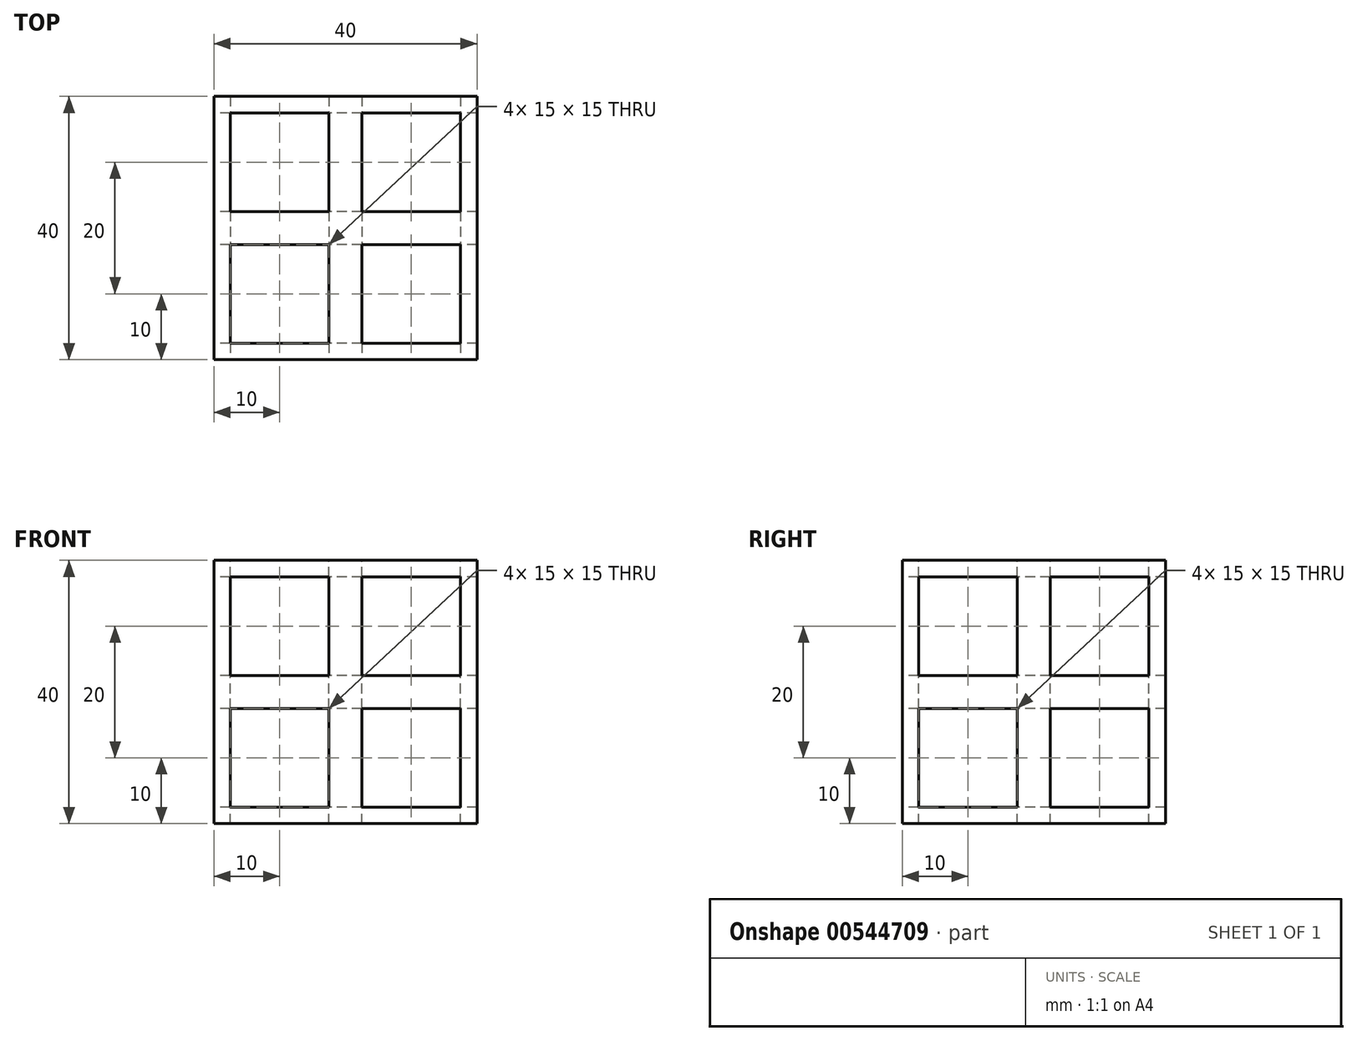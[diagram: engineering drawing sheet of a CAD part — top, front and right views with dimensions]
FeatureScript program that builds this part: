
annotation { "Feature Type Name" : "Feature", "Feature Type Description" : "" }
export const myFeature = defineFeature(function(context is Context, id is Id, definition is map)
    precondition{}
    {
        {
            var Q0;
            Q0=qCreatedBy(makeId("Front.planeOp"),FACE);
            var sketch = newSketch(context, id + "F0", { "sketchPlane" : qUnion([Q0])});
            skLineSegment(sketch, "E0.bottom", {"start": v(20, -20) * mm, "end": v(-20, -20) * mm});
            skLineSegment(sketch, "E0.top", {"start": v(20, 20) * mm, "end": v(-20, 20) * mm});
            skLineSegment(sketch, "E0.left", {"start": v(20, -20) * mm, "end": v(20, 20) * mm});
            skLineSegment(sketch, "E0.right", {"start": v(-20, -20) * mm, "end": v(-20, 20) * mm});
            skPoint(sketch, "E0.middle", {"position": v(0, 0) * mm});
            skSolve(sketch);
        }
        {
            var Q0;
            Q0=makeQuery(id+"F0.imprint","IMPRINT",FACE,{"disambiguationData":[TD([[makeQuery(id+"F0.imprint","IMPRINT",EDGE,{"derivedFrom":sQuery(id+"F0.wireOp",EDGE,"E0.bottom")}),-1.0]])]});
            extrude(context, id + "F1", {"entities" : qUnion([Q0]), "depth" : 40 * mm, "offsetDistance" : 25 * mm});
        }
        {
            var Q0;
            Q0=makeQuery(id+"F1.opExtrude","CAP_FACE",FACE,{"disambiguationData":[OSD([sQuery(id+"F0.wireOp",EDGE,"E0.bottom"),sQuery(id+"F0.wireOp",EDGE,"E0.top"),sQuery(id+"F0.wireOp",EDGE,"E0.left"),sQuery(id+"F0.wireOp",EDGE,"E0.right")])],"isStart":false});
            var sketch = newSketch(context, id + "F2", { "sketchPlane" : qUnion([Q0])});
            skPoint(sketch, "E1", {"position": v(-10, 10) * mm});
            skPoint(sketch, "E2", {"position": v(10, 10) * mm});
            skPoint(sketch, "E3", {"position": v(10, -10) * mm});
            skPoint(sketch, "E4", {"position": v(-10, -10) * mm});
            skLineSegment(sketch, "E5.bottom", {"start": v(-2.5, 2.5) * mm, "end": v(-17.5, 2.5) * mm});
            skLineSegment(sketch, "E5.top", {"start": v(-2.5, 17.5) * mm, "end": v(-17.5, 17.5) * mm});
            skLineSegment(sketch, "E5.left", {"start": v(-2.5, 2.5) * mm, "end": v(-2.5, 17.5) * mm});
            skLineSegment(sketch, "E5.right", {"start": v(-17.5, 2.5) * mm, "end": v(-17.5, 17.5) * mm});
            skLineSegment(sketch, "E6.bottom", {"start": v(17.5, 2.5) * mm, "end": v(2.5, 2.5) * mm});
            skLineSegment(sketch, "E6.top", {"start": v(17.5, 17.5) * mm, "end": v(2.5, 17.5) * mm});
            skLineSegment(sketch, "E6.left", {"start": v(17.5, 2.5) * mm, "end": v(17.5, 17.5) * mm});
            skLineSegment(sketch, "E6.right", {"start": v(2.5, 2.5) * mm, "end": v(2.5, 17.5) * mm});
            skLineSegment(sketch, "E7.bottom", {"start": v(-2.5, -17.5) * mm, "end": v(-17.5, -17.5) * mm});
            skLineSegment(sketch, "E7.top", {"start": v(-2.5, -2.5) * mm, "end": v(-17.5, -2.5) * mm});
            skLineSegment(sketch, "E7.left", {"start": v(-2.5, -17.5) * mm, "end": v(-2.5, -2.5) * mm});
            skLineSegment(sketch, "E7.right", {"start": v(-17.5, -17.5) * mm, "end": v(-17.5, -2.5) * mm});
            skLineSegment(sketch, "E8.bottom", {"start": v(17.5, -17.5) * mm, "end": v(2.5, -17.5) * mm});
            skLineSegment(sketch, "E8.top", {"start": v(17.5, -2.5) * mm, "end": v(2.5, -2.5) * mm});
            skLineSegment(sketch, "E8.left", {"start": v(17.5, -17.5) * mm, "end": v(17.5, -2.5) * mm});
            skLineSegment(sketch, "E8.right", {"start": v(2.5, -17.5) * mm, "end": v(2.5, -2.5) * mm});
            skSolve(sketch);
        }
        {
            var Q0;
            Q0=makeQuery(id+"F2.imprint","IMPRINT",FACE,{"disambiguationData":[TD([[makeQuery(id+"F2.imprint","IMPRINT",EDGE,{"derivedFrom":sQuery(id+"F2.wireOp",EDGE,"E5.bottom")}),-1.0]])]});
            var Q1;
            Q1=makeQuery(id+"F2.imprint","IMPRINT",FACE,{"disambiguationData":[TD([[makeQuery(id+"F2.imprint","IMPRINT",EDGE,{"derivedFrom":sQuery(id+"F2.wireOp",EDGE,"E6.bottom")}),-1.0]])]});
            var Q2;
            Q2=makeQuery(id+"F2.imprint","IMPRINT",FACE,{"disambiguationData":[TD([[makeQuery(id+"F2.imprint","IMPRINT",EDGE,{"derivedFrom":sQuery(id+"F2.wireOp",EDGE,"E7.bottom")}),-1.0]])]});
            var Q3;
            Q3=makeQuery(id+"F2.imprint","IMPRINT",FACE,{"disambiguationData":[TD([[makeQuery(id+"F2.imprint","IMPRINT",EDGE,{"derivedFrom":sQuery(id+"F2.wireOp",EDGE,"E8.bottom")}),-1.0]])]});
            extrude(context, id + "F3", {"entities" : qUnion([Q0, Q1, Q2, Q3]), "operationType" : NewBodyOperationType.REMOVE, "endBound" : BoundingType.THROUGH_ALL, "oppositeDirection" : true, "depth" : 25 * mm, "offsetDistance" : 25 * mm});
        }
        {
            var Q0;
            Q0=makeQuery(id+"F1.opExtrude","SWEPT_FACE",FACE,{"disambiguationData":[OSD([sQuery(id+"F0.wireOp",EDGE,"E0.right")])]});
            var sketch = newSketch(context, id + "F4", { "sketchPlane" : qUnion([Q0])});
            skPoint(sketch, "E9", {"position": v(10, 10) * mm});
            skPoint(sketch, "E10", {"position": v(30, 10) * mm});
            skPoint(sketch, "E11", {"position": v(30, -10) * mm});
            skPoint(sketch, "E12", {"position": v(10, -10) * mm});
            skLineSegment(sketch, "E13.bottom", {"start": v(17.5, 2.5) * mm, "end": v(2.5, 2.5) * mm});
            skLineSegment(sketch, "E13.top", {"start": v(17.5, 17.5) * mm, "end": v(2.5, 17.5) * mm});
            skLineSegment(sketch, "E13.left", {"start": v(17.5, 2.5) * mm, "end": v(17.5, 17.5) * mm});
            skLineSegment(sketch, "E13.right", {"start": v(2.5, 2.5) * mm, "end": v(2.5, 17.5) * mm});
            skLineSegment(sketch, "E14.bottom", {"start": v(37.5, 2.5) * mm, "end": v(22.5, 2.5) * mm});
            skLineSegment(sketch, "E14.top", {"start": v(37.5, 17.5) * mm, "end": v(22.5, 17.5) * mm});
            skLineSegment(sketch, "E14.left", {"start": v(37.5, 2.5) * mm, "end": v(37.5, 17.5) * mm});
            skLineSegment(sketch, "E14.right", {"start": v(22.5, 2.5) * mm, "end": v(22.5, 17.5) * mm});
            skLineSegment(sketch, "E15.bottom", {"start": v(17.5, -17.5) * mm, "end": v(2.5, -17.5) * mm});
            skLineSegment(sketch, "E15.top", {"start": v(17.5, -2.5) * mm, "end": v(2.5, -2.5) * mm});
            skLineSegment(sketch, "E15.left", {"start": v(17.5, -17.5) * mm, "end": v(17.5, -2.5) * mm});
            skLineSegment(sketch, "E15.right", {"start": v(2.5, -17.5) * mm, "end": v(2.5, -2.5) * mm});
            skLineSegment(sketch, "E16.bottom", {"start": v(37.5, -17.5) * mm, "end": v(22.5, -17.5) * mm});
            skLineSegment(sketch, "E16.top", {"start": v(37.5, -2.5) * mm, "end": v(22.5, -2.5) * mm});
            skLineSegment(sketch, "E16.left", {"start": v(37.5, -17.5) * mm, "end": v(37.5, -2.5) * mm});
            skLineSegment(sketch, "E16.right", {"start": v(22.5, -17.5) * mm, "end": v(22.5, -2.5) * mm});
            skSolve(sketch);
        }
        {
            var Q0;
            Q0=makeQuery(id+"F4.imprint","IMPRINT",FACE,{"disambiguationData":[TD([[makeQuery(id+"F4.imprint","IMPRINT",EDGE,{"derivedFrom":sQuery(id+"F4.wireOp",EDGE,"E13.bottom")}),-1.0]])]});
            var Q1;
            Q1=makeQuery(id+"F4.imprint","IMPRINT",FACE,{"disambiguationData":[TD([[makeQuery(id+"F4.imprint","IMPRINT",EDGE,{"derivedFrom":sQuery(id+"F4.wireOp",EDGE,"E14.bottom")}),-1.0]])]});
            var Q2;
            Q2=makeQuery(id+"F4.imprint","IMPRINT",FACE,{"disambiguationData":[TD([[makeQuery(id+"F4.imprint","IMPRINT",EDGE,{"derivedFrom":sQuery(id+"F4.wireOp",EDGE,"E15.bottom")}),-1.0]])]});
            var Q3;
            Q3=makeQuery(id+"F4.imprint","IMPRINT",FACE,{"disambiguationData":[TD([[makeQuery(id+"F4.imprint","IMPRINT",EDGE,{"derivedFrom":sQuery(id+"F4.wireOp",EDGE,"E16.bottom")}),-1.0]])]});
            extrude(context, id + "F5", {"entities" : qUnion([Q0, Q1, Q2, Q3]), "operationType" : NewBodyOperationType.REMOVE, "endBound" : BoundingType.THROUGH_ALL, "oppositeDirection" : true, "depth" : 25 * mm, "offsetDistance" : 25 * mm});
        }
        {
            var Q0;
            Q0=makeQuery(id+"F1.opExtrude","SWEPT_FACE",FACE,{"disambiguationData":[OSD([sQuery(id+"F0.wireOp",EDGE,"E0.top")])]});
            var sketch = newSketch(context, id + "F6", { "sketchPlane" : qUnion([Q0])});
            skPoint(sketch, "E17", {"position": v(-10, -10) * mm});
            skPoint(sketch, "E18", {"position": v(10, -10) * mm});
            skPoint(sketch, "E19", {"position": v(10, -30) * mm});
            skPoint(sketch, "E20", {"position": v(-10, -30) * mm});
            skLineSegment(sketch, "E21.bottom", {"start": v(-2.5, -17.5) * mm, "end": v(-17.5, -17.5) * mm});
            skLineSegment(sketch, "E21.top", {"start": v(-2.5, -2.5) * mm, "end": v(-17.5, -2.5) * mm});
            skLineSegment(sketch, "E21.left", {"start": v(-2.5, -17.5) * mm, "end": v(-2.5, -2.5) * mm});
            skLineSegment(sketch, "E21.right", {"start": v(-17.5, -17.5) * mm, "end": v(-17.5, -2.5) * mm});
            skLineSegment(sketch, "E22.bottom", {"start": v(17.5, -17.5) * mm, "end": v(2.5, -17.5) * mm});
            skLineSegment(sketch, "E22.top", {"start": v(17.5, -2.5) * mm, "end": v(2.5, -2.5) * mm});
            skLineSegment(sketch, "E22.left", {"start": v(17.5, -17.5) * mm, "end": v(17.5, -2.5) * mm});
            skLineSegment(sketch, "E22.right", {"start": v(2.5, -17.5) * mm, "end": v(2.5, -2.5) * mm});
            skLineSegment(sketch, "E23.bottom", {"start": v(-2.5, -37.5) * mm, "end": v(-17.5, -37.5) * mm});
            skLineSegment(sketch, "E23.top", {"start": v(-2.5, -22.5) * mm, "end": v(-17.5, -22.5) * mm});
            skLineSegment(sketch, "E23.left", {"start": v(-2.5, -37.5) * mm, "end": v(-2.5, -22.5) * mm});
            skLineSegment(sketch, "E23.right", {"start": v(-17.5, -37.5) * mm, "end": v(-17.5, -22.5) * mm});
            skLineSegment(sketch, "E24.bottom", {"start": v(17.5, -37.5) * mm, "end": v(2.5, -37.5) * mm});
            skLineSegment(sketch, "E24.top", {"start": v(17.5, -22.5) * mm, "end": v(2.5, -22.5) * mm});
            skLineSegment(sketch, "E24.left", {"start": v(17.5, -37.5) * mm, "end": v(17.5, -22.5) * mm});
            skLineSegment(sketch, "E24.right", {"start": v(2.5, -37.5) * mm, "end": v(2.5, -22.5) * mm});
            skSolve(sketch);
        }
        {
            var Q0;
            Q0=makeQuery(id+"F6.imprint","IMPRINT",FACE,{"disambiguationData":[TD([[makeQuery(id+"F6.imprint","IMPRINT",EDGE,{"derivedFrom":sQuery(id+"F6.wireOp",EDGE,"E21.bottom")}),-1.0]])]});
            var Q1;
            Q1=makeQuery(id+"F6.imprint","IMPRINT",FACE,{"disambiguationData":[TD([[makeQuery(id+"F6.imprint","IMPRINT",EDGE,{"derivedFrom":sQuery(id+"F6.wireOp",EDGE,"E22.bottom")}),-1.0]])]});
            var Q2;
            Q2=makeQuery(id+"F6.imprint","IMPRINT",FACE,{"disambiguationData":[TD([[makeQuery(id+"F6.imprint","IMPRINT",EDGE,{"derivedFrom":sQuery(id+"F6.wireOp",EDGE,"E23.bottom")}),-1.0]])]});
            var Q3;
            Q3=makeQuery(id+"F6.imprint","IMPRINT",FACE,{"disambiguationData":[TD([[makeQuery(id+"F6.imprint","IMPRINT",EDGE,{"derivedFrom":sQuery(id+"F6.wireOp",EDGE,"E24.bottom")}),-1.0]])]});
            extrude(context, id + "F7", {"entities" : qUnion([Q0, Q1, Q2, Q3]), "operationType" : NewBodyOperationType.REMOVE, "endBound" : BoundingType.THROUGH_ALL, "oppositeDirection" : true, "depth" : 25 * mm, "offsetDistance" : 25 * mm});
        }
    });
